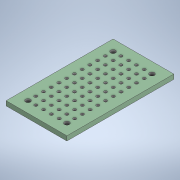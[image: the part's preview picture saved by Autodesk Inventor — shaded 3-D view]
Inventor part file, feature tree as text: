
AUTODESK INVENTOR PART (.ipt)
format: ipt  version: 2021 (Build 250183000, 183)  size: 189,440 bytes
history: native  units: mm
features: sketch x2, hole x2, extrude x1, pattern_linear x1
ambient origin geometry x8: Origin, YZ Plane, XZ Plane, XY Plane, X Axis, Y Axis, Z Axis, Center Point
bodies: Volumenkörper1 (feature_tree)
feature tree (6):
  sketch  "Skizze1"  dims[d0=12.8mm d1=28.0mm]
  extrude  "Extrusion1"  Depth=28.0mm
  hole  "Bohrung1"  [1 undecoded]
  pattern_linear  "Rechteckige Anordnung1"  Spacing1=3.6mm  [1 undecoded]
  hole  "Bohrung2"  [1 undecoded]
  sketch  "Skizze2"  dims[d2=20.0mm d3=3.6mm d4=3.6mm d5=1.5mm d6=0.0mm d7=1.0mm d8=6.0mm d9=4.0mm d10=2.0mm d11=90.0deg d12=8.0mm d13=20.594885mm d14=120.0mm d16=2.545455mm d17=60.0mm d19=2.56mm d20=1.6mm d21=6.0mm d22=4.0mm d23=2.0mm d24=90.0deg d25=8.0mm d26=20.594885mm]
note: 3 required parameter values undecoded (feature->parameter linkage not recoverable at this tier; creation-order binding heuristic only, values carry confidence <= 0.55)
